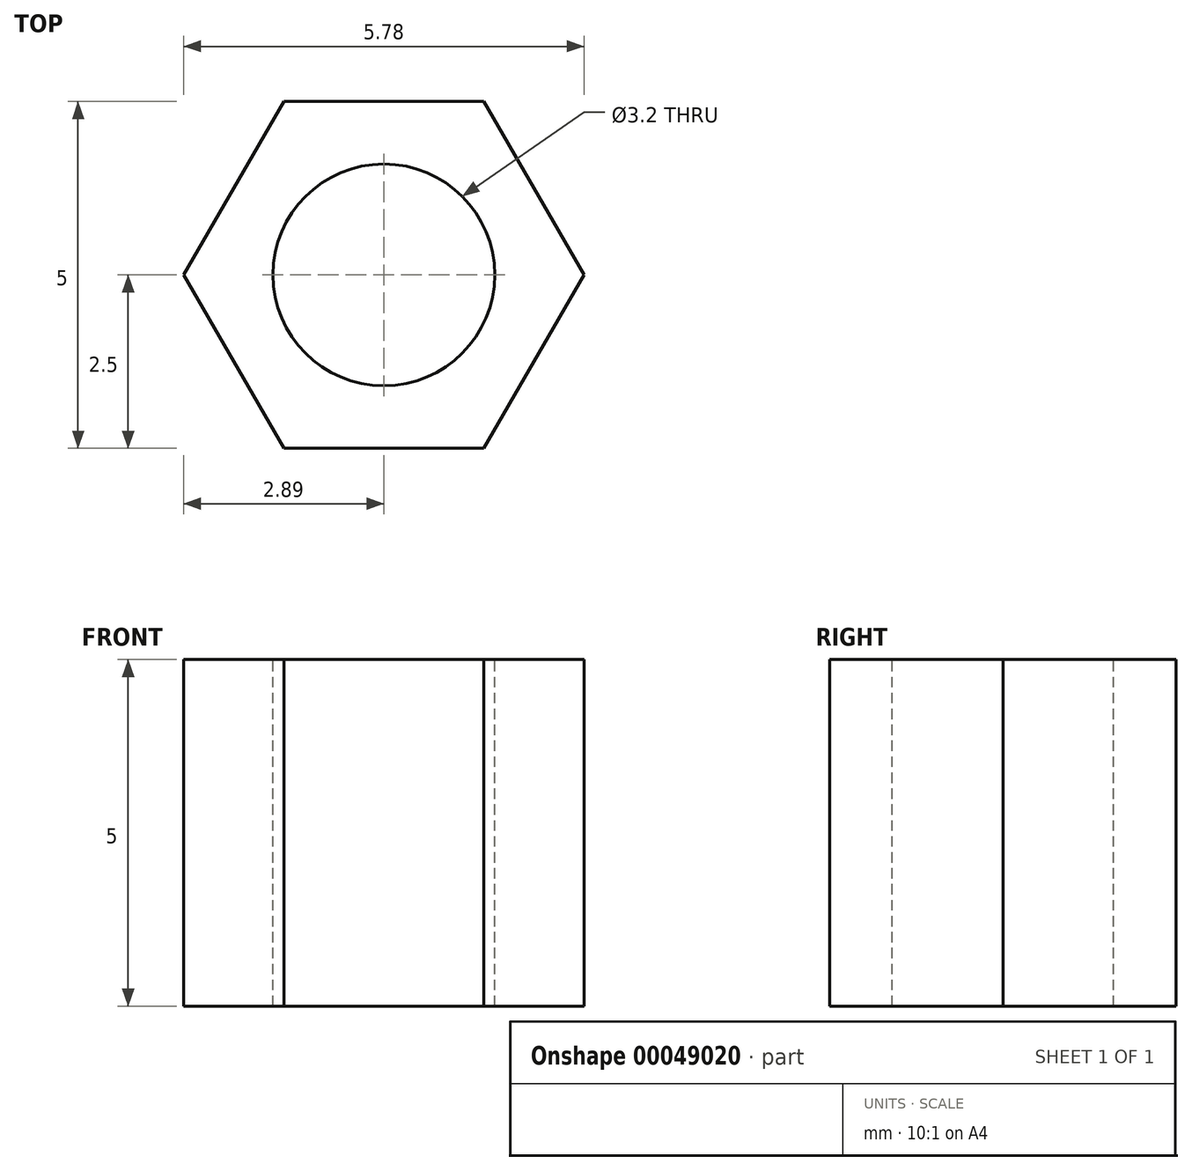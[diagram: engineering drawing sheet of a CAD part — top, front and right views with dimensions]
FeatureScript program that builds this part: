
annotation { "Feature Type Name" : "Feature", "Feature Type Description" : "" }
export const myFeature = defineFeature(function(context is Context, id is Id, definition is map)
    precondition{}
    {
        {
            var Q0;
            Q0=qCreatedBy(makeId("Top.planeOp"),FACE);
            var sketch = newSketch(context, id + "F0", { "sketchPlane" : qUnion([Q0])});
            skLineSegment(sketch, "E0", {"start": v(0, 0) * mm, "end": v(-1.44, 2.5) * mm});
            skLineSegment(sketch, "E1", {"start": v(0, 0) * mm, "end": v(0, 2.5) * mm, "construction": true});
            skLineSegment(sketch, "E2", {"start": v(-1.44, 2.5) * mm, "end": v(1.44, 2.5) * mm});
            skLineSegment(sketch, "E3", {"start": v(1.44, 2.5) * mm, "end": v(0, 0) * mm});
            skSolve(sketch);
        }
        {
            var Q0;
            Q0 = qSketchRegion(id + "F0", true);
            extrude(context, id + "F1", {"entities" : qUnion([Q0]), "depth" : 5 * mm});
        }
        {
            var Q0;
            Q0=makeQuery(id+"F1.opExtrude","SWEPT_BODY",BODY,{"disambiguationData":[OSD([sQuery(id+"F0.wireOp",EDGE,"E0"),sQuery(id+"F0.wireOp",EDGE,"E2"),sQuery(id+"F0.wireOp",EDGE,"E3")])]});
            var Q1;
            Q1=makeQuery(id+"F1.opExtrude","SWEPT_EDGE",EDGE,{"disambiguationData":[OSD([sQuery(id+"F0.wireOp",EDGE,"E0"),sQuery(id+"F0.wireOp",EDGE,"E3")])]});
            circularPattern(context, id + "F2", {"operationType" : NewBodyOperationType.ADD, "entities" : qUnion([Q0]), "axis" : qUnion([Q1]), "angle" : 300 * degree, "instanceCount" : 6, "equalSpace" : true});
        }
        {
            var Q0;
            {var subQ0=makeQuery(id+"F1.opExtrude","CAP_FACE",FACE,{"disambiguationData":[OSD([sQuery(id+"F0.wireOp",EDGE,"E0"),sQuery(id+"F0.wireOp",EDGE,"E2"),sQuery(id+"F0.wireOp",EDGE,"E3")])],"isStart":false});Q0=makeQuery(id+"F2.boolean.opBoolean","MERGE",FACE,{"derivedFrom":[subQ0,makeQuery(id+"F2.opPattern","COPY",FACE,{"derivedFrom":subQ0,"instanceName":"1"}),makeQuery(id+"F2.opPattern","COPY",FACE,{"derivedFrom":subQ0,"instanceName":"2"}),makeQuery(id+"F2.opPattern","COPY",FACE,{"derivedFrom":subQ0,"instanceName":"3"}),makeQuery(id+"F2.opPattern","COPY",FACE,{"derivedFrom":subQ0,"instanceName":"4"}),makeQuery(id+"F2.opPattern","COPY",FACE,{"derivedFrom":subQ0,"instanceName":"5"})]});}
            var sketch = newSketch(context, id + "F3", { "sketchPlane" : qUnion([Q0])});
            skCircle(sketch, "E4", {"center": v(0, 0) * mm, "radius": 1.6 * mm});
            skSolve(sketch);
        }
        {
            var Q0;
            Q0 = qSketchRegion(id + "F3", true);
            extrude(context, id + "F4", {"entities" : qUnion([Q0]), "operationType" : NewBodyOperationType.REMOVE, "endBound" : BoundingType.THROUGH_ALL, "oppositeDirection" : true, "depth" : 25 * mm});
        }
    });
